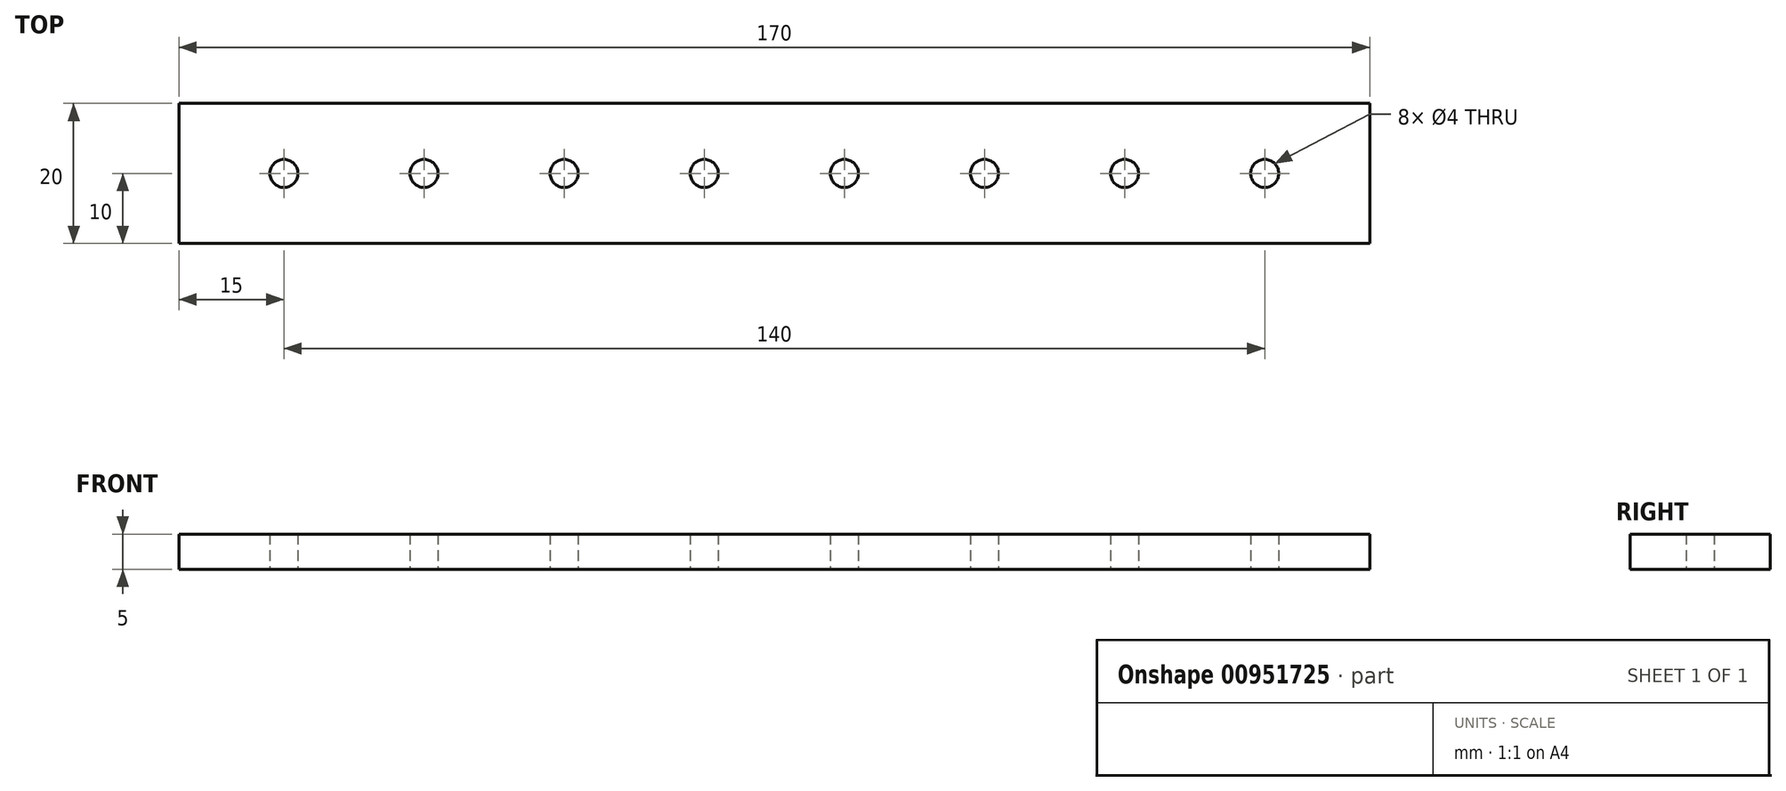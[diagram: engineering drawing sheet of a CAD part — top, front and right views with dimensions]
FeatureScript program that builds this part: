
annotation { "Feature Type Name" : "Feature", "Feature Type Description" : "" }
export const myFeature = defineFeature(function(context is Context, id is Id, definition is map)
    precondition{}
    {
        {
            var Q0;
            Q0=qCreatedBy(makeId("Top.planeOp"),FACE);
            var sketch = newSketch(context, id + "F0", { "sketchPlane" : qUnion([Q0])});
            skLineSegment(sketch, "E0.bottom", {"start": v(-85, 10) * mm, "end": v(85, 10) * mm});
            skLineSegment(sketch, "E0.top", {"start": v(-85, -10) * mm, "end": v(85, -10) * mm});
            skLineSegment(sketch, "E0.left", {"start": v(-85, 10) * mm, "end": v(-85, -10) * mm});
            skLineSegment(sketch, "E0.right", {"start": v(85, 10) * mm, "end": v(85, -10) * mm});
            skLineSegment(sketch, "E1", {"start": v(-85, 0) * mm, "end": v(85, 0) * mm, "construction": true});
            skLineSegment(sketch, "E2", {"start": v(0, 10) * mm, "end": v(0, -10) * mm, "construction": true});
            skLineSegment(sketch, "E3", {"start": v(0, 0) * mm, "end": v(10, 0) * mm});
            skCircle(sketch, "E4", {"center": v(10, 0) * mm, "radius": 2 * mm});
            skCircle(sketch, "E5.MirrorC", {"center": v(-10, 0) * mm, "radius": 2 * mm});
            skLineSegment(sketch, "E6", {"start": v(10, 0) * mm, "end": v(20, 0) * mm});
            skLineSegment(sketch, "E7", {"start": v(20, 10) * mm, "end": v(20, -10) * mm, "construction": true});
            skCircle(sketch, "E8.MirrorC", {"center": v(30, 0) * mm, "radius": 2 * mm});
            skCircle(sketch, "E9.MirrorC", {"center": v(50, 0) * mm, "radius": 2 * mm});
            skCircle(sketch, "E10.MirrorC", {"center": v(-30, 0) * mm, "radius": 2 * mm});
            skCircle(sketch, "E11.MirrorC", {"center": v(-50, 0) * mm, "radius": 2 * mm});
            skCircle(sketch, "E12.MirrorC", {"center": v(70, 0) * mm, "radius": 2 * mm});
            skCircle(sketch, "E13.MirrorC", {"center": v(-70, 0) * mm, "radius": 2 * mm});
            skSolve(sketch);
        }
        {
            var Q0;
            Q0=makeQuery(id+"F0.imprint","IMPRINT",FACE,{"disambiguationData":[TD([[makeQuery(id+"F0.imprint","IMPRINT",EDGE,{"derivedFrom":sQuery(id+"F0.wireOp",EDGE,"E0.bottom")}),-1.0]])]});
            extrude(context, id + "F1", {"entities" : qUnion([Q0]), "depth" : 5 * mm, "offsetDistance" : 25 * mm});
        }
    });
